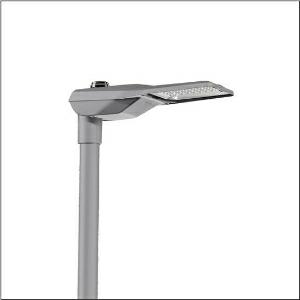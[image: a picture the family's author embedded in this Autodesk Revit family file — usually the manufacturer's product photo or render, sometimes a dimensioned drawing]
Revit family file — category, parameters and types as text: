
# Revit family: streetlight_sl_21_mini___st0_8a_5xe6c47n08gb_7d6b
name_source: partatom
category: Lighting Fixtures
units: mm (PartAtom-declared; Revit-internal decimal feet)

## family parameters
Cut with Voids When Loaded = No
Host = Face
Light Source = No
Part Type = Normal
Room Calculation Point = No
Round Connector Dimension = Use Diameter
Shared = No

## types (1)
- --- (1 x LED, 6180 lm, 40.4 W, 4000K)
    Apparent Load = 40 VA
    CIE Flux Codes = 38 75 97 100 100
    Color Rendering = 70
    Color Temperature = 4000K
    Default Elevation = 1800 mm
    Description = Streetlight SL 21 mini, mast luminaire, primary light control with lens, of PMMA, primary optical cover: cover, of toughened safety glass, transparent, light distribution: ST0.8a, light emission: direct distribution, primary light characteristic: asymmetric, installation type: side-entry, LED, 3G 1.5mm², High Power LED, rated luminous flux: 6.180lm, luminous efficacy: 153lm/W, light colour: 740, colour temperature: 4000K, control gear: NEMA (7pin), control: overheat protection, pre-setting: linear dimming characteristic, constant luminous flux control, time-dependent luminous flux control, flexible luminous flux parameterisation, mains connection: 230..240V, AC, 50/60Hz, connection cable pre-assembled, cable length: 8,5m, wiring characteristics: H07RN-F, start of lifetime: 40W, end of service life: 41W, reduction: 19W, luminaire housing, of diecast aluminium (EN AC-44300), powder-coated, Siteco® metallic grey (DB 702S), corrosivity category C5 mid according to DIN EN ISO 12944, multi-level sealing system, sealing non-destructively replaceable, inclination adjustable: 0°, 5°, 10°, 15°, length: 628mm, width: 235mm, height: 110mm, spigot size: 42mm (side-entry), mounting height: 4..8m, protection rating (complete): IP66, insulation class (complete): insulation class I (protective earthing), certification: CE, ENEC, ENEC+, VDE, impact resistance: IK10, permissible operating ambient temperature for outdoor applications: -40..+50°C, standard-compliant lighting for roads and squares, packaging unit: 1 piece

Light Distribution: ST0.8a
    Height = 110 mm
    Lamp = 1 x LED
    Lamp Light Flux = 6180 lm
    Lamp Power = 40.4 W
    Lamp count = 1
    Length = 625 mm
    Luminous efficacy = 153 lm/W
    Manufacturer = Siteco
    ModVariant = No
    Model = 5XE6C47N08GB
    Number of Poles = 1
    OnlyDefault = Yes
    Power Factor = 1
    Product Name = Streetlight SL 21 mini | ST0.8a
    Product group = mast luminaire | pylon top
    ProductGroupID = 6100
    Protection Class = Protection class I
    Protection Degree = IP 66
    RLX_Detail_Level = 1
    RLX_Emergency_Light_Flux = 0 lm
    RLX_Emergency_Type = 0
    RLX_Emergency_Type_DB = No
    RlxData = <blob elided: 25865 chars, md5=1a344375>
    Socket = socket
    Standby Power = 0 W
    System Light Flux = 6180 lm
    System Power = 40 W
    Type Comments = factory setting: luminous flux: 100 % | dim-lin: 254 | 812 mA
    Type Image = l_1294379.jpg
    URL = http://relux.com
    VarID = @adj_155667
    Voltage = 0 V
    Weight = 0.00 kg
    Width = 234 mm

## geometry (parser evidence)
native form markers: Blend x4, Sweep x11
no freeform markers — native parametric forms only
